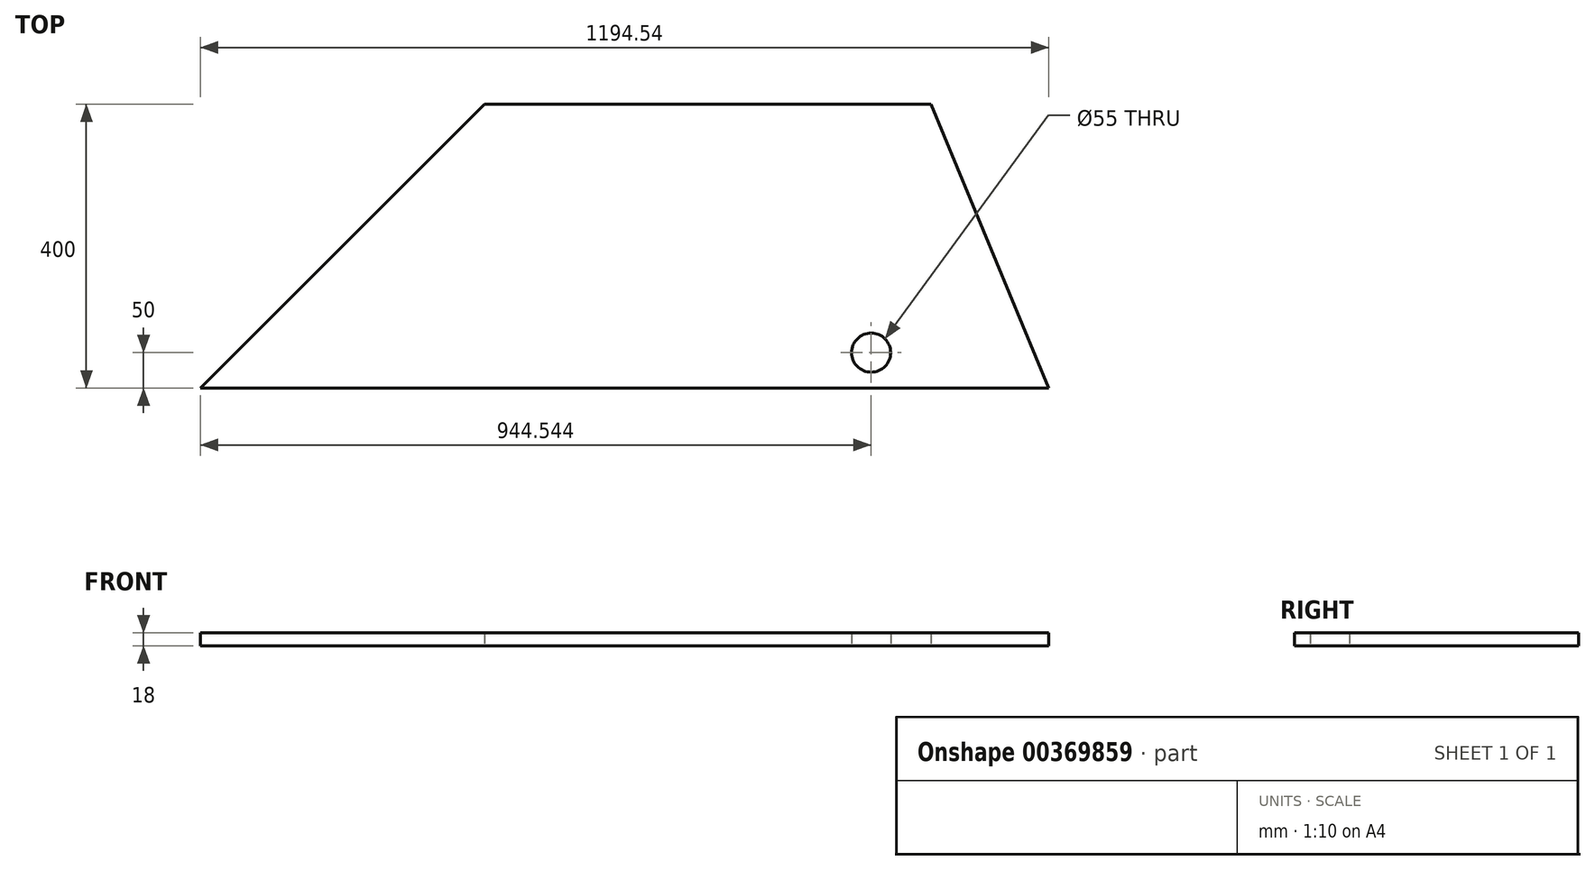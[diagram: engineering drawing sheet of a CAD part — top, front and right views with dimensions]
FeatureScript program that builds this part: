
annotation { "Feature Type Name" : "Feature", "Feature Type Description" : "" }
export const myFeature = defineFeature(function(context is Context, id is Id, definition is map)
    precondition{}
    {
        {
            var Q0;
            Q0=qCreatedBy(makeId("Top.planeOp"),FACE);
            var sketch = newSketch(context, id + "F0", { "sketchPlane" : qUnion([Q0])});
            skLineSegment(sketch, "E0", {"start": v(0, 0) * mm, "end": v(1194.54, 0) * mm});
            skLineSegment(sketch, "E1", {"start": v(1194.54, 0) * mm, "end": v(1592.32, 397.78) * mm, "construction": true});
            skLineSegment(sketch, "E2", {"start": v(400, 400) * mm, "end": v(0, 0) * mm});
            skLineSegment(sketch, "E3", {"start": v(1592.32, 397.78) * mm, "end": v(1309.48, 680.62) * mm, "construction": true});
            skLineSegment(sketch, "E4", {"start": v(1309.48, 680.62) * mm, "end": v(1028.86, 400) * mm, "construction": true});
            skLineSegment(sketch, "E5", {"start": v(1028.86, 400) * mm, "end": v(400, 400) * mm});
            skLineSegment(sketch, "E6", {"start": v(1605.05, 385.05) * mm, "end": v(1202, -18) * mm, "construction": true});
            skLineSegment(sketch, "E7", {"start": v(1202, -18) * mm, "end": v(-18, -18) * mm, "construction": true});
            skLineSegment(sketch, "E8", {"start": v(-30.73, -5.27) * mm, "end": v(374.54, 400) * mm, "construction": true});
            skLineSegment(sketch, "E9", {"start": v(-30.73, -5.27) * mm, "end": v(-18, -18) * mm, "construction": true});
            skLineSegment(sketch, "E10", {"start": v(-18, -18) * mm, "end": v(-18, -18) * mm});
            skCircle(sketch, "E11", {"center": v(944.54, 50) * mm, "radius": 27.5 * mm});
            skLineSegment(sketch, "E12", {"start": v(1028.86, 400) * mm, "end": v(1194.54, 0) * mm});
            skSolve(sketch);
        }
        {
            var Q0;
            Q0=makeQuery(id+"F0.imprint","IMPRINT",FACE,{"disambiguationData":[TD([[makeQuery(id+"F0.imprint","IMPRINT",EDGE,{"derivedFrom":sQuery(id+"F0.wireOp",EDGE,"E0")}),1.0]])]});
            extrude(context, id + "F1", {"entities" : qUnion([Q0]), "depth" : 18 * mm});
        }
    });
